# Revit family: apollon_r__21_linear_51mq17wd2312_219c
name_source: partatom
category: Lighting Fixtures
units: mm (PartAtom-declared; Revit-internal decimal feet)

## family parameters
Cut with Voids When Loaded = No
Host = Face
Light Source = No
Part Type = Normal
Room Calculation Point = No
Round Connector Dimension = Use Diameter
Shared = No

## types (1)
- Apollon® 21 linear (1 x LED, 6900 lm, 60 W, 3000K)
    Apparent Load = 60 VA
    CIE Flux Codes = 61 87 97 100 100
    Color Rendering = 80
    Color Temperature = 3000K
    Default Elevation = 1800 mm
    Description = Apollon® 21 linear, office luminaire, primary optical cover: micro prismatic cover, CAT 2 (L<= 3000cd/m²), light emission: direct distribution, primary light characteristic: symmetric, installation type: lay-in mounting, LED, rated luminous flux: 6.900lm, luminous efficacy: 115lm/W, light colour: 830, colour temperature: 3000K, control gear: ECG DALI, with terminal, 5-pole, mains connection: 220..240V, AC, 50/60Hz, rated input power: 60W, housing, of aluminium, coated, pure white, length: 1.545mm, width: 307mm, height: 39mm, housing upper side, of sheet steel, galvanised, protection rating (complete): IP20, protection rating (lamp compartment, on room side): IP50, insulation class (complete): insulation class II (safety insulation), certification: CE, ENEC, packaging unit: 1 piece
    Height = 0 mm  [stored 0 ft]
    Lamp = 1 x LED
    Lamp Light Flux = 6900 lm
    Lamp Power = 60 W
    Lamp count = 1
    Length = 1545 mm
    Luminous efficacy = 115 lm/W
    Manufacturer = Siteco
    ModVariant = No
    Model = 51MQ17WD2312
    Mounting Place = Ceiling
    Mounting Type = Recessed
    Number of Poles = 1
    OnlyDefault = Yes
    Power Factor = 1
    Product Name = Apollon® 21 linear
    Product group = office luminaire | ceiling recessed
    ProductGroupID = 400
    Protection Class = Protection class II
    Protection Degree = IP 20
    RLX_Detail_Level = 1
    RlxData = <blob elided: 17245 chars, md5=0d40a29d>
    Socket = socket
    Standby Power = 0 W
    System Light Flux = 6900 lm
    System Power = 60 W
    Type Comments = Product without accessories
    Type Image = l_1004243.jpg
    URL = http://relux.com
    VarID = ---
    Voltage = 0 V
    Weight = 0.00 kg
    Width = 307 mm

note: [stored X ft] marks values corroborated as IEEE doubles in the binary element streams (Revit-internal decimal feet)

## geometry (parser evidence)
native form markers: Blend x4, Sweep x11
no freeform markers — native parametric forms only
